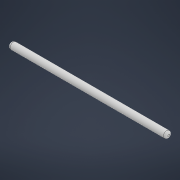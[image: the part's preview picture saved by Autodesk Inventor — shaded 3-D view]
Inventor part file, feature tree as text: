
AUTODESK INVENTOR PART (.ipt)
format: ipt  version: 2022 (Build 260153000, 153)  size: 96,256 bytes
history: native  units: mm
features: fillet x2, other x1, extrude x1, sketch x1
ambient origin geometry x8: Origin, YZ Plane, XZ Plane, XY Plane, X Axis, Y Axis, Z Axis, Center Point
bodies: Body1 (feature_tree)
feature tree (5):
  other  "Твердое тело1"
  extrude  "Выдавливание1"  Depth=3.0mm
  fillet  "Сопряжение1"  Radius=72.0mm
  fillet  "Сопряжение2"  Radius=1.0mm
  sketch  "Эскиз1"
